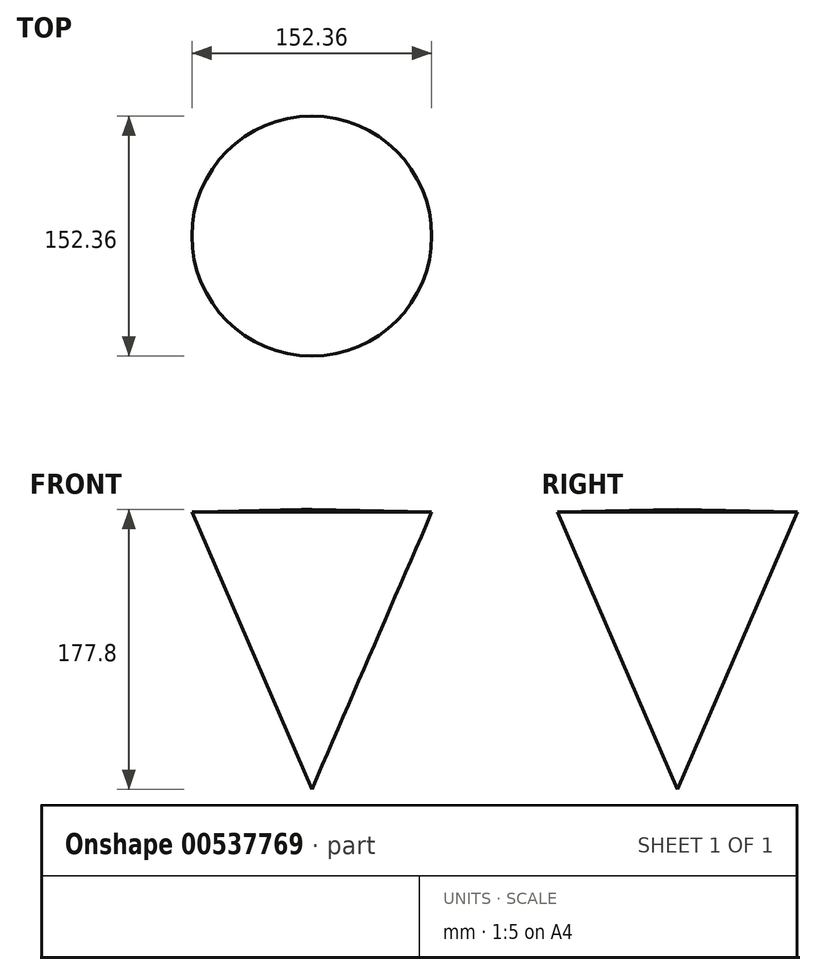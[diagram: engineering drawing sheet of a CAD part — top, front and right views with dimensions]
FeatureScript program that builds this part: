
annotation { "Feature Type Name" : "Feature", "Feature Type Description" : "" }
export const myFeature = defineFeature(function(context is Context, id is Id, definition is map)
    precondition{}
    {
        {
            var Q0;
            Q0=qCreatedBy(makeId("Front.planeOp"),FACE);
            var sketch = newSketch(context, id + "F0", { "sketchPlane" : qUnion([Q0])});
            skLineSegment(sketch, "E0", {"start": v(0, 89.55) * mm, "end": v(0, -88.25) * mm});
            skLineSegment(sketch, "E1", {"start": v(0, -88.25) * mm, "end": v(76.18, 87.82) * mm});
            skLineSegment(sketch, "E2", {"start": v(76.18, 87.82) * mm, "end": v(0, 89.55) * mm});
            skSolve(sketch);
        }
        {
            var Q0;
            Q0=makeQuery(id+"F0.imprint","IMPRINT",FACE,{"disambiguationData":[TD([[makeQuery(id+"F0.imprint","IMPRINT",EDGE,{"derivedFrom":sQuery(id+"F0.wireOp",EDGE,"E0")}),1.0]])]});
            var Q1;
            Q1=sQuery(id+"F0.wireOp",EDGE,"E0");
            revolve(context, id + "F1", {"entities" : qUnion([Q0]), "axis" : qUnion([Q1]), "revolveType" : RevolveType.FULL});
        }
    });
